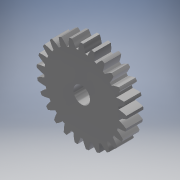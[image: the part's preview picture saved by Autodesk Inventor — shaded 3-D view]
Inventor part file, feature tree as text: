
AUTODESK INVENTOR PART (.ipt)
format: ipt  version: 2019 (Build 230136000, 136)  size: 251,904 bytes
history: native  units: mm (DEFAULTED — no unit token found)
features: plane x3, other x3, sketch x3, extrude x1, hole x1
ambient origin geometry x8: Origin, YZ Plane, XZ Plane, XY Plane, X Axis, Y Axis, Z Axis, Center Point
bodies: Solid1 (feature_tree)
feature tree (11):
  extrude  "Extrusion1"  Depth=2.5mm TaperAngle=0.0deg
  plane  "Work Plane2"
  plane  "Work Plane8"
  plane  "Work Plane9"
  other  "Przekładnia walcowa"
  hole  "Otwór1"  [1 undecoded]
  sketch  "Sketch1"  dims[d0=13.5mm d1=2.5mm d2=0.0mm]
  sketch  "Sketch2"  dims[d3=12.5mm d4=10.0mm d5=0.0mm d16=8.75mm d17=0.0mm d34=1.256637mm d39=0.0mm d41=0.0mm d43=8.75mm d46=8.75mm d47=0.0mm d48=0.0mm d49=2.5mm d50=6.0mm d51=4.0mm d52=2.0mm d53=90.0deg d54=8.0mm d55=20.594885mm]
  other  "Srf1"
  sketch  "Szkic3"
  other  "Średnica podziałowa"
note: 1 required parameter value undecoded (feature->parameter linkage not recoverable at this tier; creation-order binding heuristic only, values carry confidence <= 0.55)
